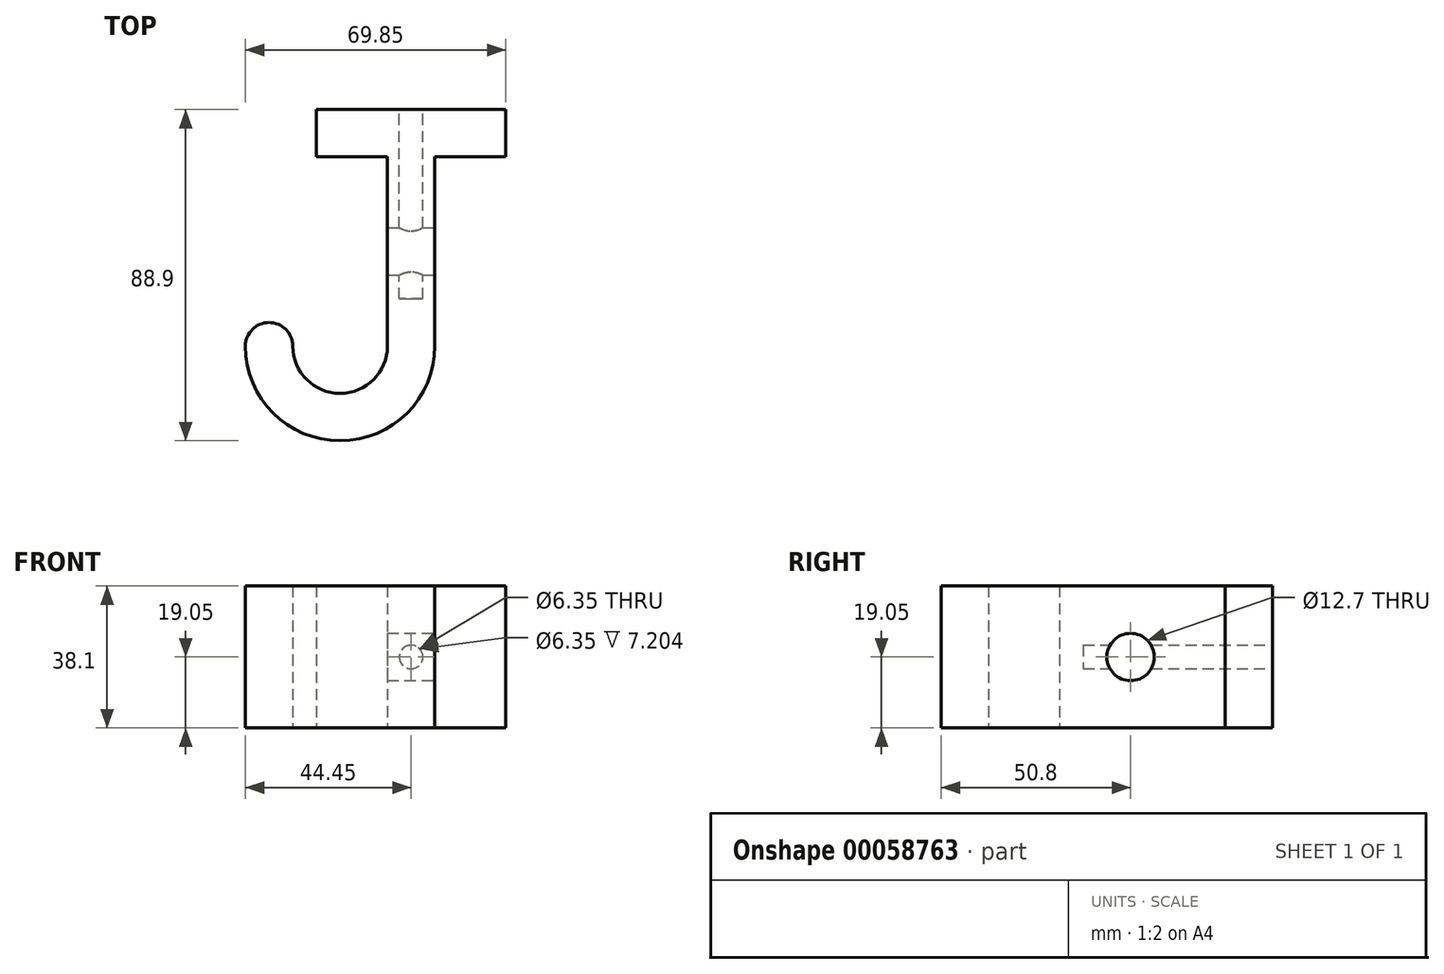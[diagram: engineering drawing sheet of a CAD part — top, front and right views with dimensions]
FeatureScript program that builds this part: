
annotation { "Feature Type Name" : "Feature", "Feature Type Description" : "" }
export const myFeature = defineFeature(function(context is Context, id is Id, definition is map)
    precondition{}
    {
        {
            var Q0;
            Q0=qCreatedBy(makeId("Top.planeOp"),FACE);
            var sketch = newSketch(context, id + "F0", { "sketchPlane" : qUnion([Q0])});
            skLineSegment(sketch, "E0.bottom", {"start": v(0, 0) * mm, "end": v(12.7, 0) * mm});
            skLineSegment(sketch, "E0.top", {"start": v(0, 50.8) * mm, "end": v(12.7, 50.8) * mm});
            skLineSegment(sketch, "E0.left", {"start": v(0, 0) * mm, "end": v(0, 50.8) * mm});
            skLineSegment(sketch, "E0.right", {"start": v(12.7, 0) * mm, "end": v(12.7, 50.8) * mm});
            skLineSegment(sketch, "E1.bottom", {"start": v(6.35, 50.8) * mm, "end": v(31.75, 50.8) * mm});
            skLineSegment(sketch, "E1.top", {"start": v(6.35, 63.5) * mm, "end": v(31.75, 63.5) * mm});
            skLineSegment(sketch, "E1.left", {"start": v(6.35, 50.8) * mm, "end": v(6.35, 63.5) * mm});
            skLineSegment(sketch, "E1.right", {"start": v(31.75, 50.8) * mm, "end": v(31.75, 63.5) * mm});
            skLineSegment(sketch, "E2.bottom", {"start": v(6.35, 50.8) * mm, "end": v(6.35, 50.8) * mm});
            skLineSegment(sketch, "E2.top", {"start": v(6.35, 63.5) * mm, "end": v(6.35, 63.5) * mm});
            skLineSegment(sketch, "E3.bottom", {"start": v(6.35, 50.8) * mm, "end": v(-19.05, 50.8) * mm});
            skLineSegment(sketch, "E3.top", {"start": v(6.35, 63.5) * mm, "end": v(-19.05, 63.5) * mm});
            skLineSegment(sketch, "E3.right", {"start": v(-19.05, 50.8) * mm, "end": v(-19.05, 63.5) * mm});
            skArc(sketch, "E4", {"start": v(-25.4, 0) * mm, "mid": v(-12.7, -12.7) * mm, "end": v(0, 0) * mm});
            skLineSegment(sketch, "E5", {"start": v(-25.4, 0) * mm, "end": v(-38.1, 0) * mm, "construction": true});
            skArc(sketch, "E6", {"start": v(-38.1, 0) * mm, "mid": v(-12.7, -25.4) * mm, "end": v(12.7, 0) * mm});
            skLineSegment(sketch, "E7", {"start": v(-31.75, 0) * mm, "end": v(-31.75, 6.35) * mm, "construction": true});
            skArc(sketch, "E8", {"start": v(-25.4, 0) * mm, "mid": v(-31.75, 6.35) * mm, "end": v(-38.1, 0) * mm});
            skLineSegment(sketch, "E9", {"start": v(-12.7, -25.4) * mm, "end": v(-12.7, 63.5) * mm, "construction": true});
            skSolve(sketch);
        }
        {
            var Q0;
            Q0 = qSketchRegion(id + "F0", true);
            extrude(context, id + "F1", {"entities" : qUnion([Q0]), "depth" : 38.1 * mm});
        }
        {
            var Q0;
            Q0=makeQuery(id+"F1.opExtrude","SWEPT_FACE",FACE,{"disambiguationData":[OSD([sQuery(id+"F0.wireOp",EDGE,"E0.right")])]});
            var sketch = newSketch(context, id + "F2", { "sketchPlane" : qUnion([Q0])});
            skCircle(sketch, "E10", {"center": v(25.4, 19.05) * mm, "radius": 6.35 * mm});
            skPoint(sketch, "E10.centerSnap0", {"position": v(25.4, 38.1) * mm});
            skPoint(sketch, "E10.centerSnap1", {"position": v(0, 19.05) * mm});
            skSolve(sketch);
        }
        {
            var Q0;
            Q0=makeQuery(id+"F2.imprint","IMPRINT",FACE,{"disambiguationData":[TD([[makeQuery(id+"F2.imprint","IMPRINT",EDGE,{"derivedFrom":sQuery(id+"F2.wireOp",EDGE,"E10")}),1.0]])]});
            extrude(context, id + "F3", {"entities" : qUnion([Q0]), "operationType" : NewBodyOperationType.REMOVE, "endBound" : BoundingType.THROUGH_ALL, "oppositeDirection" : true, "depth" : 25.4 * mm});
        }
        {
            var Q0;
            Q0=makeQuery(id+"F1.opExtrude","SWEPT_FACE",FACE,{"disambiguationData":[OSD([sQuery(id+"F0.wireOp",EDGE,"E1.top"),sQuery(id+"F0.wireOp",EDGE,"E3.top")])]});
            var sketch = newSketch(context, id + "F4", { "sketchPlane" : qUnion([Q0])});
            skCircle(sketch, "E11", {"center": v(-6.35, 19.05) * mm, "radius": 3.18 * mm});
            skPoint(sketch, "E11.centerSnap0", {"position": v(-31.75, 19.05) * mm});
            skPoint(sketch, "E11.centerSnap1", {"position": v(-6.35, 38.1) * mm});
            skLineSegment(sketch, "E12", {"start": v(-31.75, 19.05) * mm, "end": v(-6.35, 19.05) * mm, "construction": true});
            skLineSegment(sketch, "E13", {"start": v(-6.35, 19.05) * mm, "end": v(-6.35, 38.1) * mm, "construction": true});
            skSolve(sketch);
        }
        {
            var Q0;
            Q0=makeQuery(id+"F4.imprint","IMPRINT",FACE,{"disambiguationData":[TD([[makeQuery(id+"F4.imprint","IMPRINT",EDGE,{"derivedFrom":sQuery(id+"F4.wireOp",EDGE,"E11")}),1.0]])]});
            extrude(context, id + "F5", {"entities" : qUnion([Q0]), "operationType" : NewBodyOperationType.REMOVE, "oppositeDirection" : true, "depth" : 50.8 * mm});
        }
    });
